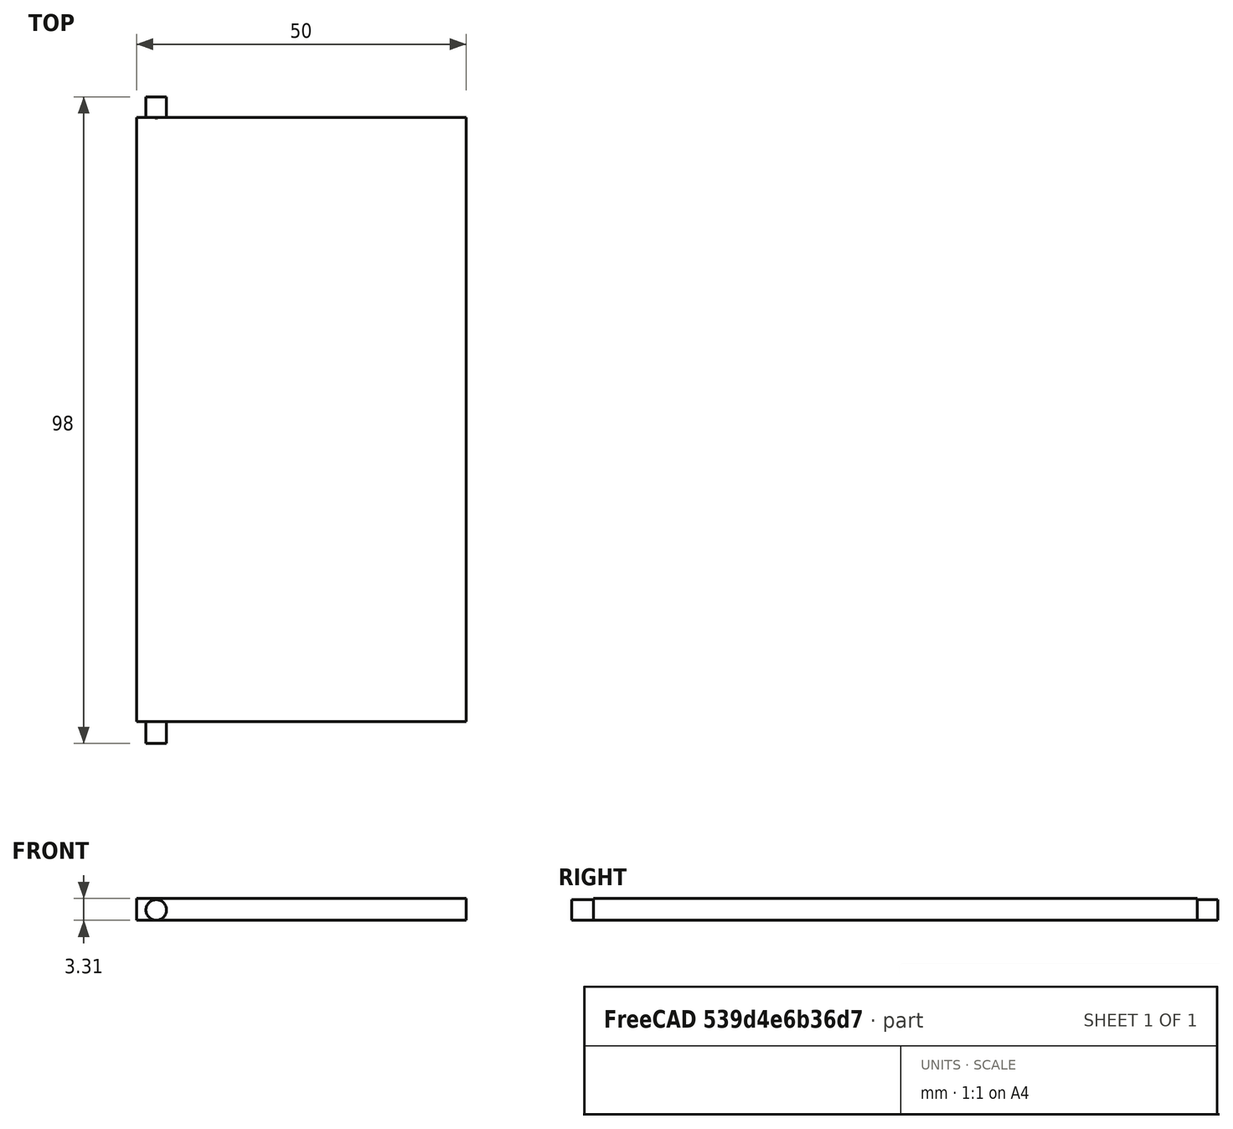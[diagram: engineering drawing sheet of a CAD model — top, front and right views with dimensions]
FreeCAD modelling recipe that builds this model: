
FCSTD DOCUMENT  (FreeCAD 0.20R29603 (Git))
Label: shuffle-flap-long
License: All rights reserved
LicenseURL: http://en.wikipedia.org/wiki/All_rights_reserved
objects: PartDesign::AdditiveCylinder×2, PartDesign::AdditiveBox×1, PartDesign::Body×1
note: 7 computed .brp shape members not serialized (recipe doc carries the construction recipe); baked Part::Feature solids carry a one-line shape summary decoded from their .brp

FEATURE [PartDesign::AdditiveBox] Box
  AttacherType = Attacher::AttachEngine3D
  Height = 3.3
  Length = 50
  Width = 91.6
FEATURE [PartDesign::AdditiveCylinder] Cylinder
  Angle = 360
  AttacherType = Attacher::AttachEngine3D
  AttachmentOffset = pos=(3,1.55,0) rot=(0,0,1;0rad)
  BaseFeature = -> Box
  FirstAngle = 0
  Height = 3.3
  MapMode = 5
  Placement = pos=(3,3e-16,1.55) rot=(1,0,0;1.5708rad)
  Radius = 1.56
  SecondAngle = 0
  Support = -> [Box]
FEATURE [PartDesign::AdditiveCylinder] Cylinder001
  Angle = 360
  AttacherType = Attacher::AttachEngine3D
  AttachmentOffset = pos=(0,0,-98) rot=(0,0,1;0rad)
  BaseFeature = -> Cylinder
  FirstAngle = 0
  Height = 3.3
  MapMode = 5
  Placement = pos=(3,94.7,1.55) rot=(1,0,0;1.5708rad)
  Radius = 1.56
  SecondAngle = 0
  Support = -> [Cylinder]
FEATURE [PartDesign::Body] Body
  Group = -> [Box,Cylinder,Cylinder001]
  Origin = -> Origin
  Tip = -> Cylinder001
